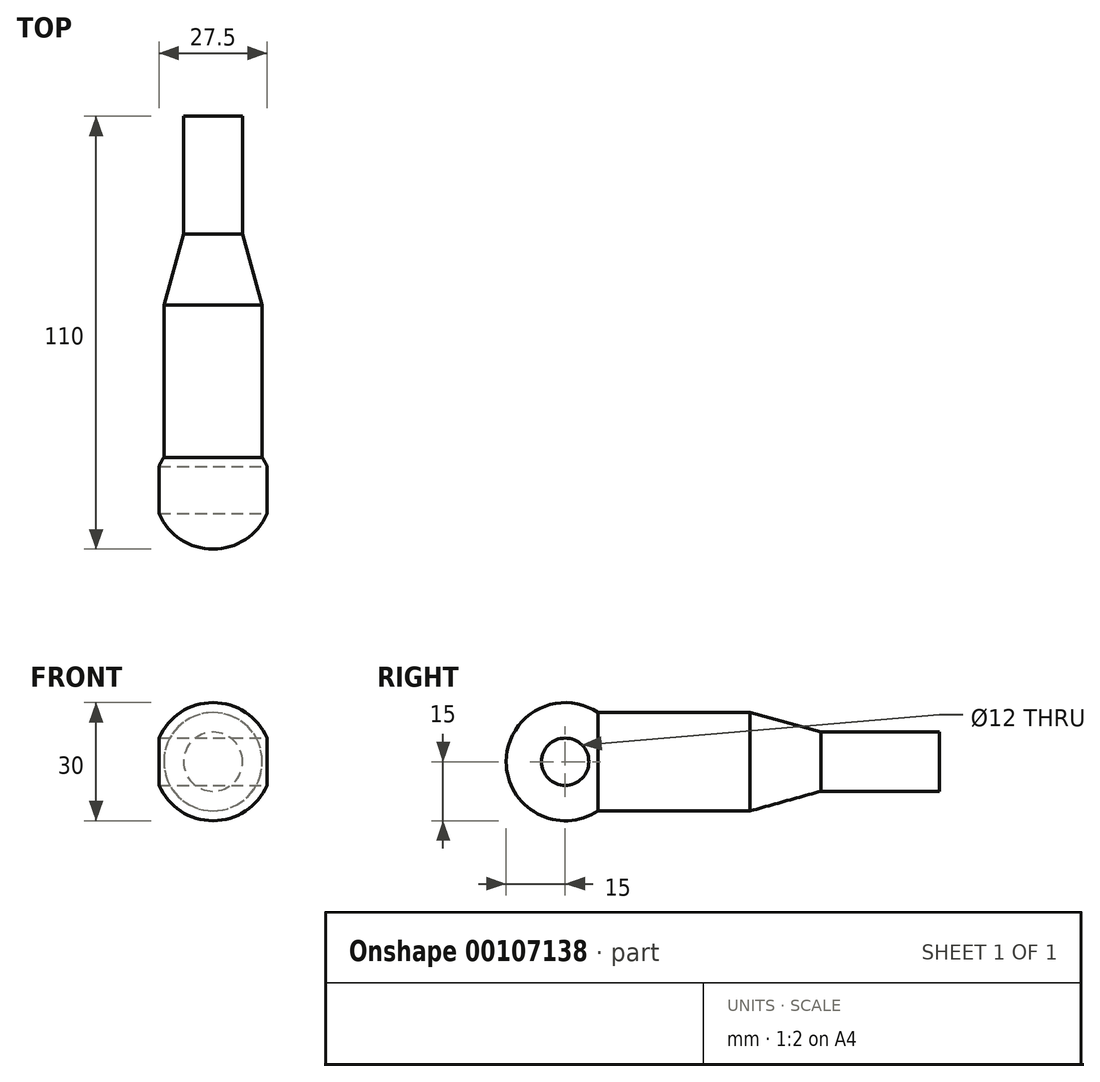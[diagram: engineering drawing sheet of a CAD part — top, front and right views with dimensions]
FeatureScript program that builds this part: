
annotation { "Feature Type Name" : "Feature", "Feature Type Description" : "" }
export const myFeature = defineFeature(function(context is Context, id is Id, definition is map)
    precondition{}
    {
        {
            var Q0;
            Q0=qCreatedBy(makeId("Right.planeOp"),FACE);
            var sketch = newSketch(context, id + "F0", { "sketchPlane" : qUnion([Q0])});
            skLineSegment(sketch, "E0", {"start": v(95, 0) * mm, "end": v(95, 7.5) * mm});
            skLineSegment(sketch, "E1", {"start": v(95, 7.5) * mm, "end": v(65, 7.5) * mm});
            skArc(sketch, "E2", {"start": v(-15, 0) * mm, "mid": v(-7.1, 13.22) * mm, "end": v(8.3, 12.5) * mm});
            skLineSegment(sketch, "E3", {"start": v(8.3, 12.5) * mm, "end": v(47, 12.5) * mm});
            skLineSegment(sketch, "E4", {"start": v(47, 12.5) * mm, "end": v(65, 7.5) * mm});
            skLineSegment(sketch, "E5", {"start": v(-15, 0) * mm, "end": v(95, 0) * mm});
            skLineSegment(sketch, "E6", {"start": v(-36.58, 0) * mm, "end": v(126.39, 0) * mm, "construction": true});
            skSolve(sketch);
        }
        {
            var Q0;
            Q0 = qSketchRegion(id + "F0", true);
            var Q1;
            Q1=sQuery(id+"F0.wireOp",EDGE,"E6");
            revolve(context, id + "F1", {"entities" : qUnion([Q0]), "axis" : qUnion([Q1]), "revolveType" : RevolveType.FULL});
        }
        {
            var Q0;
            Q0=qCreatedBy(makeId("Right.planeOp"),FACE);
            var sketch = newSketch(context, id + "F2", { "sketchPlane" : qUnion([Q0])});
            skCircle(sketch, "E7", {"center": v(0, 0) * mm, "radius": 6 * mm});
            skSolve(sketch);
        }
        {
            var Q0;
            Q0 = qSketchRegion(id + "F2", true);
            extrude(context, id + "F3", {"entities" : qUnion([Q0]), "operationType" : NewBodyOperationType.REMOVE, "endBound" : BoundingType.SYMMETRIC, "oppositeDirection" : true, "depth" : 76.87 * mm});
        }
    });
